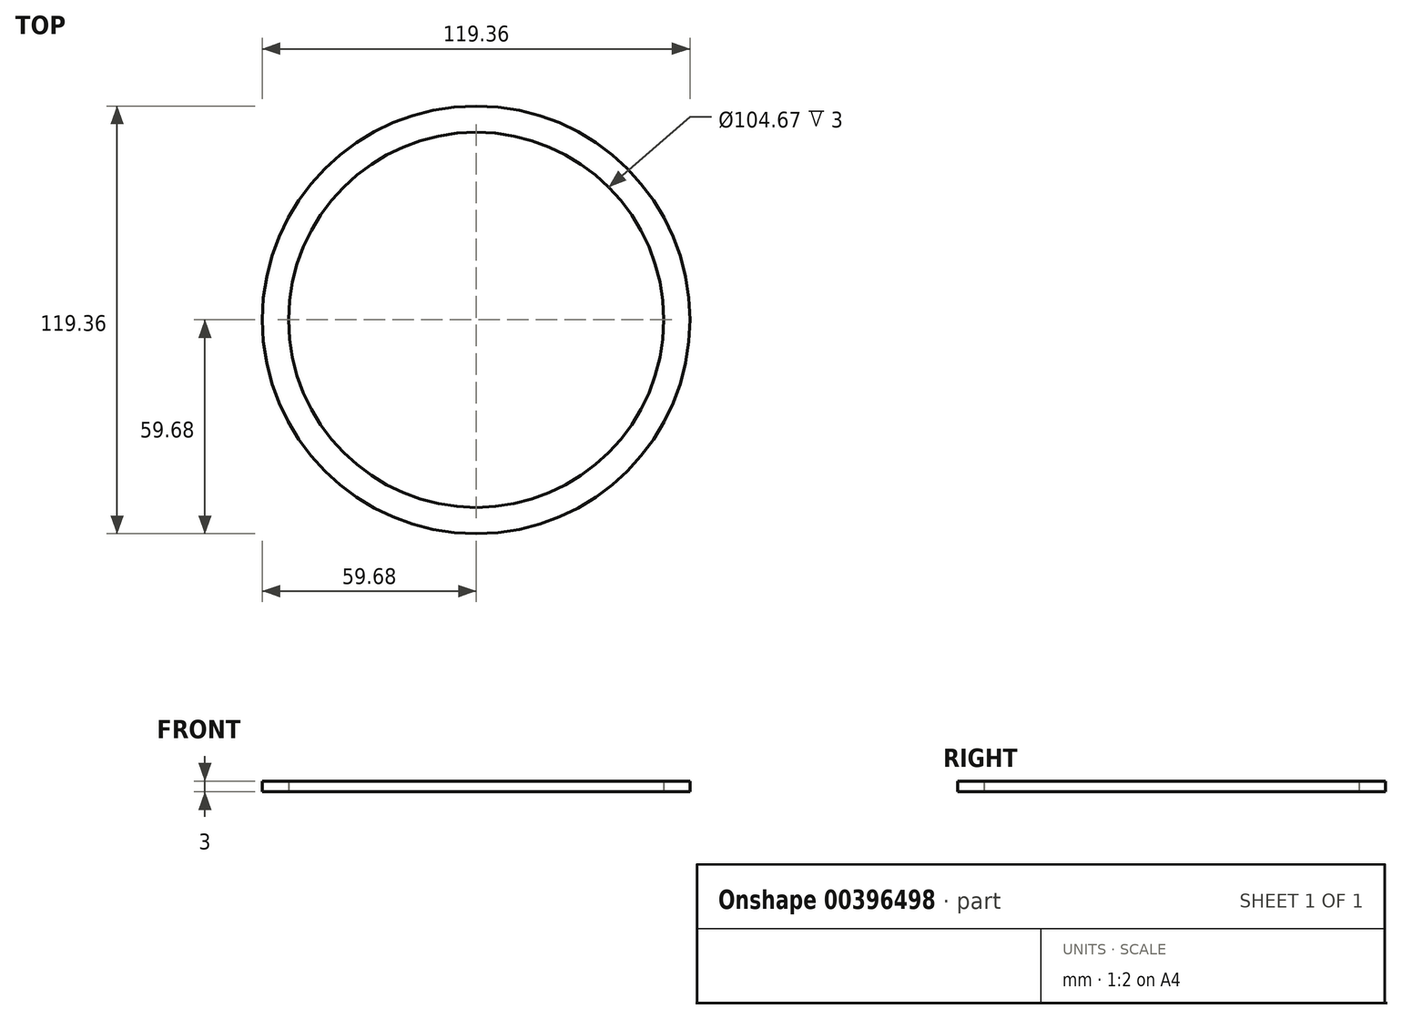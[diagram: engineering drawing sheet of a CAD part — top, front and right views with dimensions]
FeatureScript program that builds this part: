
annotation { "Feature Type Name" : "Feature", "Feature Type Description" : "" }
export const myFeature = defineFeature(function(context is Context, id is Id, definition is map)
    precondition{}
    {
        {
            var Q0;
            Q0=qCreatedBy(makeId("Top.planeOp"),FACE);
            var sketch = newSketch(context, id + "F0", { "sketchPlane" : qUnion([Q0])});
            skCircle(sketch, "E0", {"center": v(0, 0) * mm, "radius": 59.68 * mm});
            skCircle(sketch, "E1", {"center": v(0, 0) * mm, "radius": 52.33 * mm});
            skSolve(sketch);
        }
        {
            var Q0;
            Q0=makeQuery(id+"F0.imprint","IMPRINT",FACE,{"disambiguationData":[TD([[makeQuery(id+"F0.imprint","IMPRINT",EDGE,{"derivedFrom":sQuery(id+"F0.wireOp",EDGE,"E0")}),1.0]])]});
            extrude(context, id + "F1", {"entities" : qUnion([Q0]), "depth" : 3 * mm});
        }
    });
